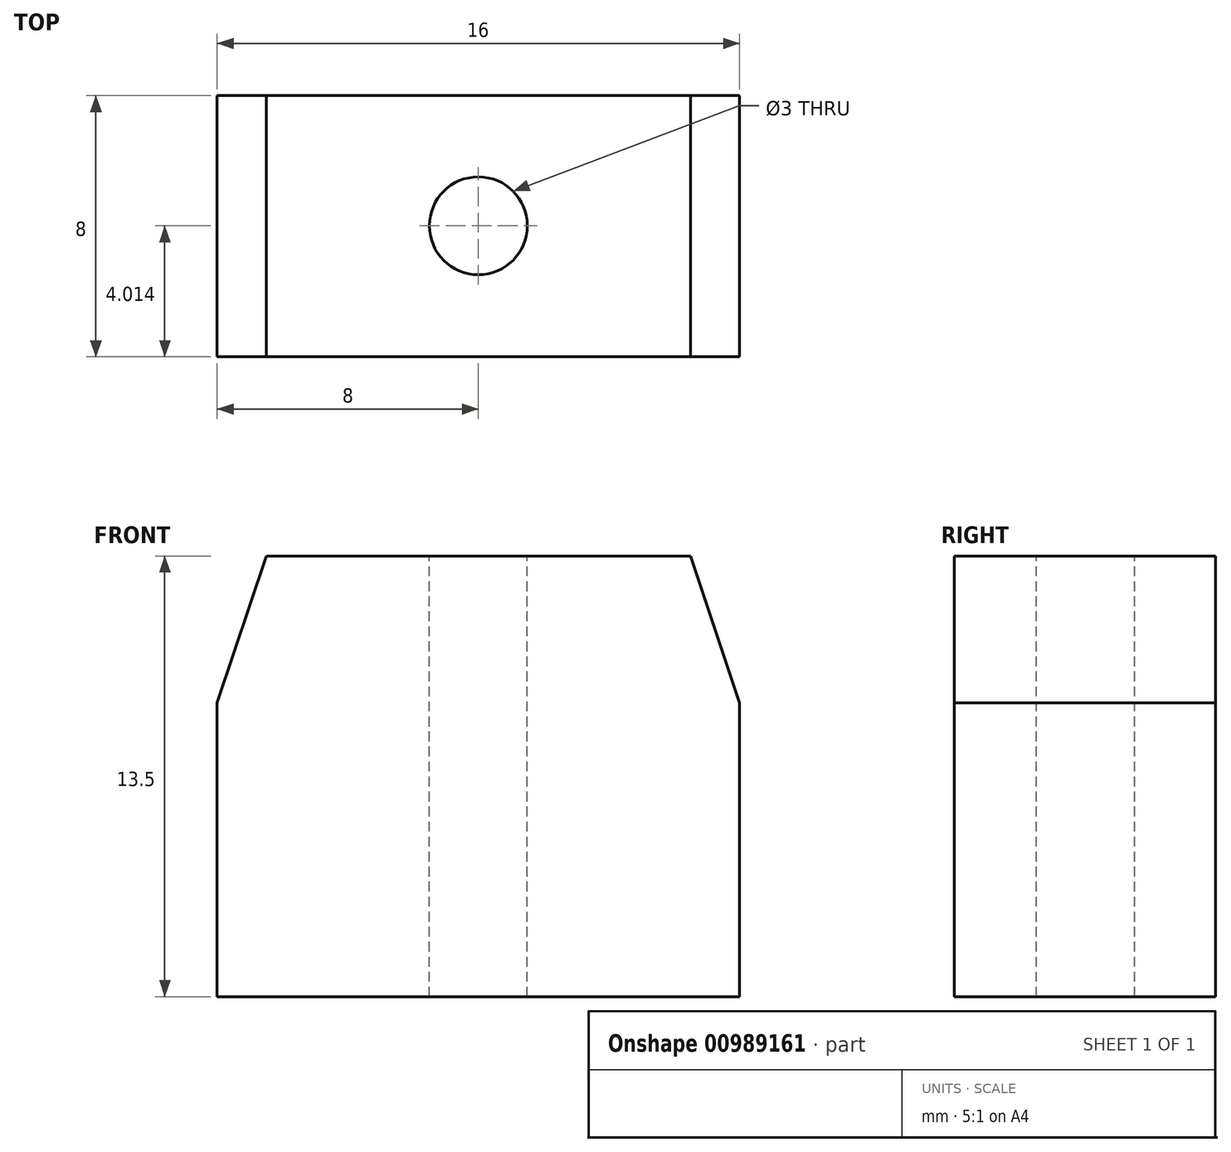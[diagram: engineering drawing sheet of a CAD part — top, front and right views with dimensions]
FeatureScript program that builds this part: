
annotation { "Feature Type Name" : "Feature", "Feature Type Description" : "" }
export const myFeature = defineFeature(function(context is Context, id is Id, definition is map)
    precondition{}
    {
        {
            var Q0;
            Q0=qCreatedBy(makeId("Front.planeOp"),FACE);
            var sketch = newSketch(context, id + "F0", { "sketchPlane" : qUnion([Q0])});
            skLineSegment(sketch, "E0", {"start": v(-8, 0) * mm, "end": v(-8, 9) * mm});
            skLineSegment(sketch, "E1", {"start": v(-8, 9) * mm, "end": v(-6.5, 13.5) * mm});
            skLineSegment(sketch, "E2", {"start": v(-6.5, 13.5) * mm, "end": v(6.5, 13.5) * mm});
            skLineSegment(sketch, "E3", {"start": v(6.5, 13.5) * mm, "end": v(8, 9) * mm});
            skLineSegment(sketch, "E4", {"start": v(8, 9) * mm, "end": v(8, 0) * mm});
            skLineSegment(sketch, "E5", {"start": v(-8, 0) * mm, "end": v(-2, 0) * mm});
            skLineSegment(sketch, "E6", {"start": v(2, 0) * mm, "end": v(8, 0) * mm});
            skLineSegment(sketch, "E7", {"start": v(-2, 0) * mm, "end": v(2, 0) * mm});
            skSolve(sketch);
        }
        {
            var Q0;
            Q0=makeQuery(id+"F0.imprint","IMPRINT",FACE,{"disambiguationData":[TD([[makeQuery(id+"F0.imprint","IMPRINT",EDGE,{"derivedFrom":sQuery(id+"F0.wireOp",EDGE,"E0")}),-1.0]])]});
            extrude(context, id + "F1", {"entities" : qUnion([Q0]), "depth" : 8 * mm, "offsetDistance" : 25 * mm});
        }
        {
            var Q0;
            Q0=makeQuery(id+"F1.opExtrude","SWEPT_FACE",FACE,{"disambiguationData":[OSD([sQuery(id+"F0.wireOp",EDGE,"E2")])]});
            var sketch = newSketch(context, id + "F2", { "sketchPlane" : qUnion([Q0])});
            skPoint(sketch, "E8", {"position": v(0, -3.99) * mm});
            skSolve(sketch);
        }
        {
            var Q0;
            Q0=sQuery(id+"F2.wireOp",VERTEX,"E8");
            var Q1;
            Q1=makeQuery(id+"F1.opExtrude","SWEPT_BODY",BODY,{"disambiguationData":[OSD([sQuery(id+"F0.wireOp",EDGE,"E0"),sQuery(id+"F0.wireOp",EDGE,"E1"),sQuery(id+"F0.wireOp",EDGE,"E2"),sQuery(id+"F0.wireOp",EDGE,"E3"),sQuery(id+"F0.wireOp",EDGE,"E4"),sQuery(id+"F0.wireOp",EDGE,"E5"),sQuery(id+"F0.wireOp",EDGE,"C935xy8k-bsZT-9lOl-ruL4-MjVH4cBlBil6"),sQuery(id+"F0.wireOp",EDGE,"Cma1KaBn-Uja4-xx0g-f6YM-Evd94ObqiwZA"),sQuery(id+"F0.wireOp",EDGE,"nxNF48Ez-w6yC-jiwR-m9oF-kYYTSi8Qs1fd"),sQuery(id+"F0.wireOp",EDGE,"E6")])]});
            hole(context, id + "F3", {"style" : HoleStyle.SIMPLE, "endStyle" : HoleEndStyle.BLIND, "holeDiameter" : 3 * mm, "majorDiameter" : 5 * mm, "holeDepth" : 20 * mm, "isTappedThrough" : true, "tappedDepth" : 12 * mm, "tapClearance" : 3, "locations" : qUnion([Q0]), "scope" : qUnion([Q1])});
        }
    });
